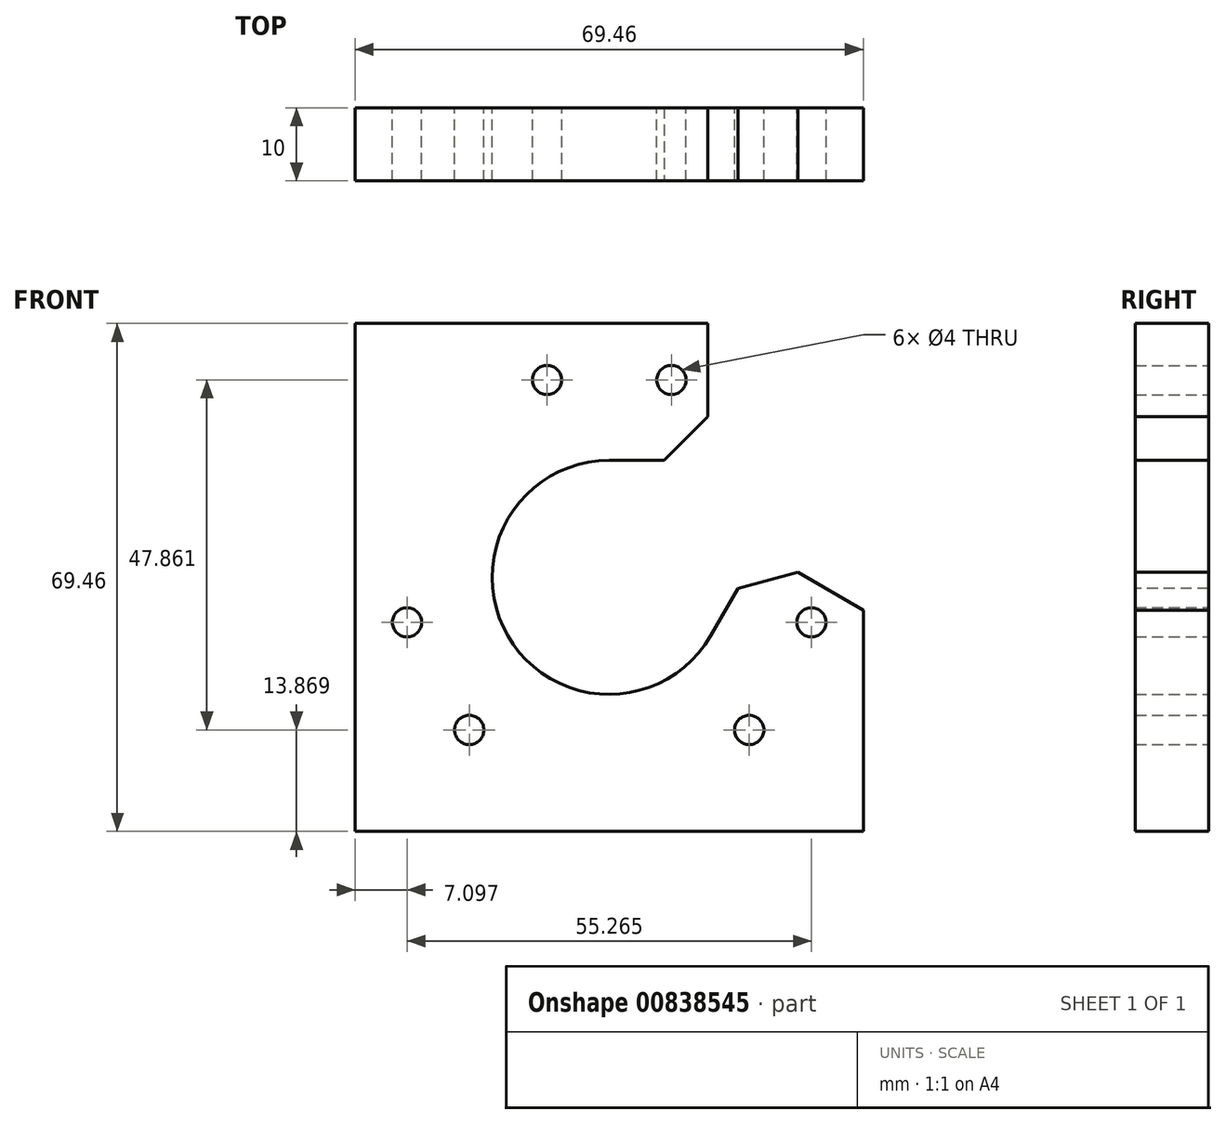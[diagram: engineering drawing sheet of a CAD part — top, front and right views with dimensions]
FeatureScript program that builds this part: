
annotation { "Feature Type Name" : "Feature", "Feature Type Description" : "" }
export const myFeature = defineFeature(function(context is Context, id is Id, definition is map)
    precondition{}
    {
        {
            var Q0;
            Q0=qCreatedBy(makeId("Front.planeOp"),FACE);
            var sketch = newSketch(context, id + "F0", { "sketchPlane" : qUnion([Q0])});
            skLineSegment(sketch, "E0.bottom", {"start": v(40, 40) * mm, "end": v(-40, 40) * mm});
            skLineSegment(sketch, "E0.top", {"start": v(40, -40) * mm, "end": v(-40, -40) * mm});
            skLineSegment(sketch, "E0.left", {"start": v(40, 40) * mm, "end": v(40, -40) * mm});
            skLineSegment(sketch, "E0.right", {"start": v(-40, 40) * mm, "end": v(-40, -40) * mm});
            skPoint(sketch, "E0.middle", {"position": v(0, 0) * mm});
            skCircle(sketch, "E1", {"center": v(0, 0) * mm, "radius": 16 * mm});
            skCircle(sketch, "E2", {"center": v(0, 0) * mm, "radius": 27 * mm, "construction": true});
            skCircle(sketch, "E3", {"center": v(8.5, 27) * mm, "radius": 2 * mm});
            skCircle(sketch, "E4", {"center": v(0, 0) * mm, "radius": 28.3 * mm, "construction": true});
            skCircle(sketch, "E5", {"center": v(-8.5, 27) * mm, "radius": 2 * mm});
            skCircle(sketch, "E6", {"center": v(-27.63, -6.14) * mm, "radius": 2 * mm});
            skCircle(sketch, "E7", {"center": v(-19.13, -20.86) * mm, "radius": 2 * mm});
            skCircle(sketch, "E8", {"center": v(19.13, -20.86) * mm, "radius": 2 * mm});
            skCircle(sketch, "E9", {"center": v(27.63, -6.14) * mm, "radius": 2 * mm});
            skLineSegment(sketch, "E10", {"start": v(-8.5, 27) * mm, "end": v(8.5, 27) * mm, "construction": true});
            skLineSegment(sketch, "E11", {"start": v(-27.63, -6.14) * mm, "end": v(-19.13, -20.86) * mm, "construction": true});
            skLineSegment(sketch, "E12", {"start": v(19.13, -20.86) * mm, "end": v(27.63, -6.14) * mm, "construction": true});
            skLineSegment(sketch, "E13", {"start": v(-23.38, -13.5) * mm, "end": v(0, 27) * mm, "construction": true});
            skLineSegment(sketch, "E14", {"start": v(0, 27) * mm, "end": v(23.38, -13.5) * mm, "construction": true});
            skLineSegment(sketch, "E15", {"start": v(-23.38, -13.5) * mm, "end": v(23.38, -13.5) * mm, "construction": true});
            skSolve(sketch);
        }
        {
            var Q0;
            Q0=makeQuery(id+"F0.imprint","IMPRINT",FACE,{"disambiguationData":[TD([[makeQuery(id+"F0.imprint","IMPRINT",EDGE,{"derivedFrom":sQuery(id+"F0.wireOp",EDGE,"E0.bottom")}),1.0]])]});
            extrude(context, id + "F1", {"entities" : qUnion([Q0]), "depth" : 10 * mm, "offsetDistance" : 25 * mm});
        }
        {
            var Q0;
            Q0=makeQuery(id+"F1.opExtrude","CAP_FACE",FACE,{"disambiguationData":[OSD([sQuery(id+"F0.wireOp",EDGE,"E0.bottom"),sQuery(id+"F0.wireOp",EDGE,"E0.top"),sQuery(id+"F0.wireOp",EDGE,"E0.left"),sQuery(id+"F0.wireOp",EDGE,"E0.right"),sQuery(id+"F0.wireOp",EDGE,"E1"),sQuery(id+"F0.wireOp",EDGE,"E3"),sQuery(id+"F0.wireOp",EDGE,"E5"),sQuery(id+"F0.wireOp",EDGE,"E6"),sQuery(id+"F0.wireOp",EDGE,"E7"),sQuery(id+"F0.wireOp",EDGE,"E8"),sQuery(id+"F0.wireOp",EDGE,"E9")])],"isStart":false});
            var sketch = newSketch(context, id + "F2", { "sketchPlane" : qUnion([Q0])});
            skLineSegment(sketch, "E16.bottom", {"start": v(-3.5, 32) * mm, "end": v(-13.5, 32) * mm, "construction": true});
            skLineSegment(sketch, "E16.top", {"start": v(-3.5, 22) * mm, "end": v(-13.5, 22) * mm, "construction": true});
            skLineSegment(sketch, "E16.left", {"start": v(-3.5, 32) * mm, "end": v(-3.5, 22) * mm, "construction": true});
            skLineSegment(sketch, "E16.right", {"start": v(-13.5, 32) * mm, "end": v(-13.5, 22) * mm, "construction": true});
            skPoint(sketch, "E16.middle", {"position": v(-8.5, 27) * mm});
            skCircle(sketch, "E17", {"center": v(0, 0) * mm, "radius": 34.73 * mm, "construction": true});
            skLineSegment(sketch, "E18.bottom", {"start": v(-34.73, 34.73) * mm, "end": v(34.73, 34.73) * mm});
            skLineSegment(sketch, "E18.top", {"start": v(-34.73, -34.73) * mm, "end": v(34.73, -34.73) * mm});
            skLineSegment(sketch, "E18.left", {"start": v(-34.73, 34.73) * mm, "end": v(-34.73, -34.73) * mm});
            skLineSegment(sketch, "E18.right", {"start": v(34.73, 34.73) * mm, "end": v(34.73, -34.73) * mm});
            skSolve(sketch);
        }
        {
            var Q0;
            Q0=makeQuery(id+"F2.imprint","IMPRINT",FACE,{"disambiguationData":[TD([[makeQuery(id+"F2.imprint","IMPRINT",EDGE,{"derivedFrom":sQuery(id+"F2.wireOp",EDGE,"E18.bottom")}),1.0]])]});
            var Q1;
            Q1=sQuery(id+"F2.wireOp",EDGE,"E18.left");
            var Q2;
            Q2=sQuery(id+"F2.wireOp",EDGE,"E18.bottom");
            var Q3;
            Q3=sQuery(id+"F2.wireOp",EDGE,"E18.right");
            var Q4;
            Q4=sQuery(id+"F2.wireOp",EDGE,"E18.top");
            extrude(context, id + "F3", {"entities" : qUnion([Q0]), "operationType" : NewBodyOperationType.REMOVE, "surfaceEntities" : qUnion([Q1, Q2, Q3, Q4]), "oppositeDirection" : true, "depth" : 25 * mm, "offsetDistance" : 25 * mm});
        }
        {
            var Q0;
            Q0=makeQuery(id+"F1.opExtrude","CAP_FACE",FACE,{"disambiguationData":[OSD([sQuery(id+"F0.wireOp",EDGE,"E0.bottom"),sQuery(id+"F0.wireOp",EDGE,"E0.top"),sQuery(id+"F0.wireOp",EDGE,"E0.left"),sQuery(id+"F0.wireOp",EDGE,"E0.right"),sQuery(id+"F0.wireOp",EDGE,"E1"),sQuery(id+"F0.wireOp",EDGE,"E3"),sQuery(id+"F0.wireOp",EDGE,"E5"),sQuery(id+"F0.wireOp",EDGE,"E6"),sQuery(id+"F0.wireOp",EDGE,"E7"),sQuery(id+"F0.wireOp",EDGE,"E8"),sQuery(id+"F0.wireOp",EDGE,"E9")])],"isStart":false});
            var sketch = newSketch(context, id + "F4", { "sketchPlane" : qUnion([Q0])});
            skLineSegment(sketch, "E19", {"start": v(19.13, -20.86) * mm, "end": v(27.63, -6.14) * mm, "construction": true});
            skLineSegment(sketch, "E20", {"start": v(0, 0) * mm, "end": v(23.38, -13.5) * mm, "construction": true});
            skLineSegment(sketch, "E21", {"start": v(25.8, 0.7) * mm, "end": v(41.85, -8.57) * mm});
            skLineSegment(sketch, "E22", {"start": v(17.34, -13.96) * mm, "end": v(29.34, 6.82) * mm, "construction": true});
            skLineSegment(sketch, "E23", {"start": v(25.8, 0.7) * mm, "end": v(17.6, -1.5) * mm});
            skLineSegment(sketch, "E24", {"start": v(13.86, -8) * mm, "end": v(17.6, -1.5) * mm});
            skLineSegment(sketch, "E25", {"start": v(13.5, 34.73) * mm, "end": v(13.5, 22) * mm});
            skLineSegment(sketch, "E26", {"start": v(13.5, 22) * mm, "end": v(7.5, 16) * mm});
            skLineSegment(sketch, "E27", {"start": v(7.5, 16) * mm, "end": v(0, 16) * mm});
            skLineSegment(sketch, "E28", {"start": v(8.5, 27) * mm, "end": v(-8.5, 27) * mm, "construction": true});
            skLineSegment(sketch, "E29", {"start": v(0, 16) * mm, "end": v(13.86, -8) * mm});
            skLineSegment(sketch, "E30", {"start": v(41.85, -8.57) * mm, "end": v(36.73, 37.05) * mm});
            skLineSegment(sketch, "E31", {"start": v(36.73, 37.05) * mm, "end": v(13.5, 34.73) * mm});
            skSolve(sketch);
        }
        {
            var Q0;
            Q0 = qSketchRegion(id + "F4", true);
            extrude(context, id + "F5", {"entities" : qUnion([Q0]), "operationType" : NewBodyOperationType.REMOVE, "oppositeDirection" : true, "depth" : 25 * mm, "offsetDistance" : 25 * mm});
        }
    });
